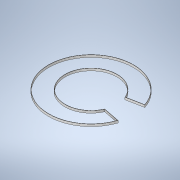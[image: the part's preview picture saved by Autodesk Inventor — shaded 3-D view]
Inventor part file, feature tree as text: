
AUTODESK INVENTOR PART (.ipt)
format: ipt  version: 2020 (Build 240168000, 168)  size: 158,720 bytes
history: native  units: mm
features: extrude x1, sketch x1
ambient origin geometry x8: Origin, YZ Plane, XZ Plane, XY Plane, X Axis, Y Axis, Z Axis, Center Point
bodies: Body1 (feature_tree)
feature tree (2):
  extrude  "Extrusion2"  Depth=30.0mm
  sketch  "Sketch1"  dims[d0=504.787567mm d1=944.787567mm d65=50.0mm d71=50.0mm d81=4.0mm d82=4.0mm d83=30.0mm d84=0.0mm]
